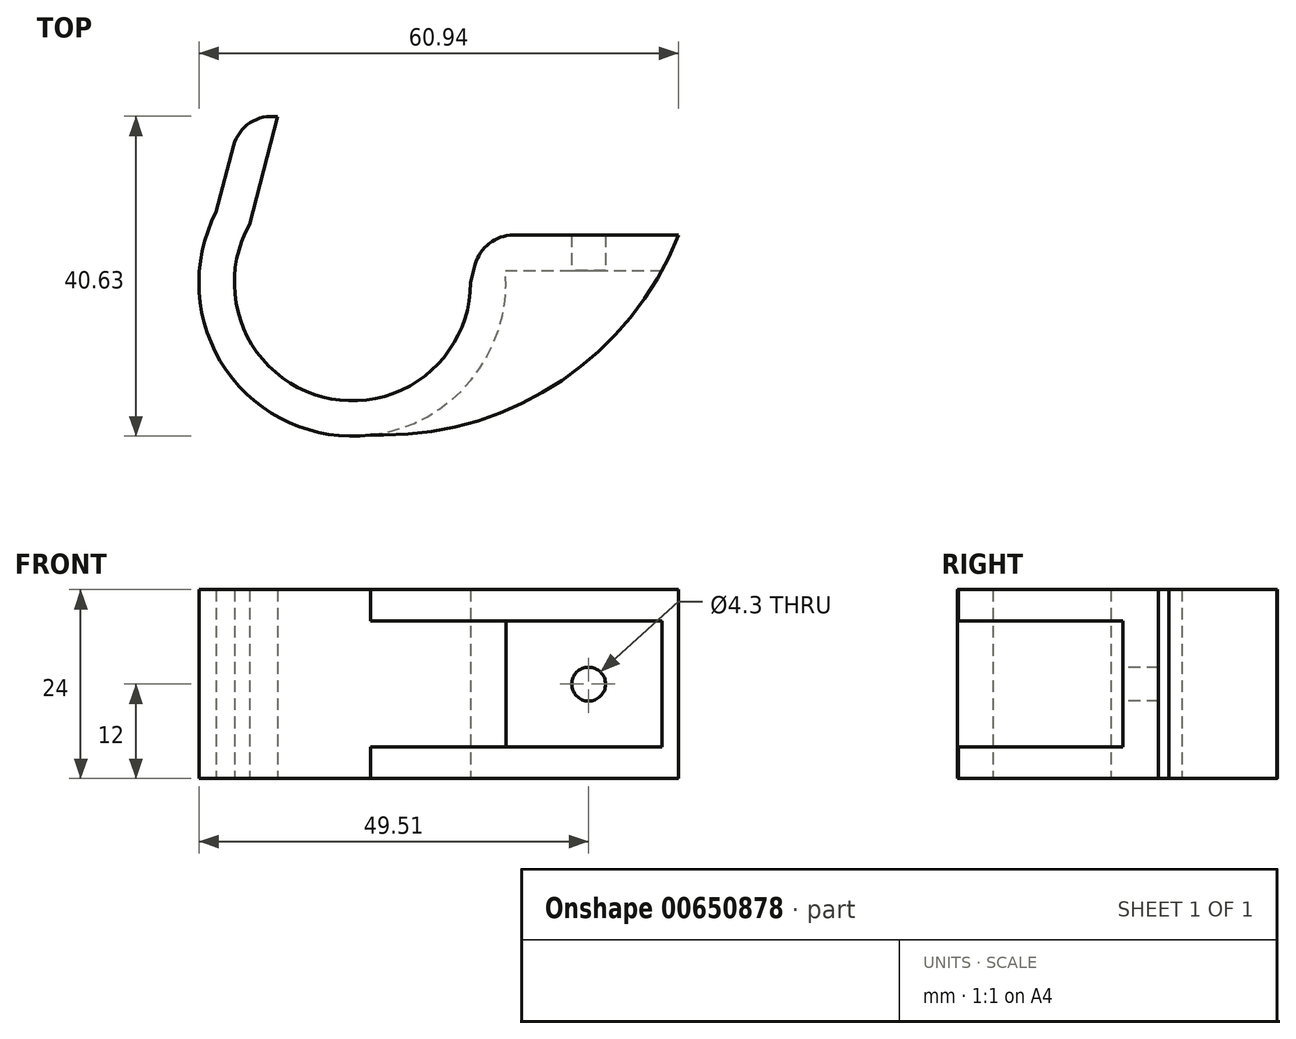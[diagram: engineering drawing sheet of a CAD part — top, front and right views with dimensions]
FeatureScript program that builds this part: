
annotation { "Feature Type Name" : "Feature", "Feature Type Description" : "" }
export const myFeature = defineFeature(function(context is Context, id is Id, definition is map)
    precondition{}
    {
        {
            var Q0;
            Q0=qCreatedBy(makeId("Top.planeOp"),FACE);
            var sketch = newSketch(context, id + "F0", { "sketchPlane" : qUnion([Q0])});
            skArc(sketch, "E0", {"start": v(-13.07, 7.36) * mm, "mid": v(-3.8, -14.5) * mm, "end": v(15, 0) * mm});
            skLineSegment(sketch, "E1", {"start": v(-13.07, 7.36) * mm, "end": v(-9.48, 21.07) * mm});
            skLineSegment(sketch, "E2", {"start": v(15, 0) * mm, "end": v(16.58, 6.03) * mm});
            skLineSegment(sketch, "E3", {"start": v(16.58, 6.03) * mm, "end": v(41.44, 6.03) * mm});
            skPoint(sketch, "E4.orphan", {"position": v(-15, 0) * mm});
            skLineSegment(sketch, "E5.0", {"start": v(-17.29, 9.02) * mm, "end": v(-13.83, 22.2) * mm});
            skArc(sketch, "E5.1", {"start": v(-17.29, 9.02) * mm, "mid": v(-3.9, -19.1) * mm, "end": v(19.44, 1.53) * mm});
            skLineSegment(sketch, "E5.2", {"start": v(19.44, 1.53) * mm, "end": v(41.44, 1.53) * mm});
            skLineSegment(sketch, "E6", {"start": v(41.44, 6.03) * mm, "end": v(41.44, 1.53) * mm});
            skLineSegment(sketch, "E7", {"start": v(-13.83, 22.2) * mm, "end": v(-9.48, 21.07) * mm});
            skSolve(sketch);
        }
        {
            var Q0;
            Q0=makeQuery(id+"F0.imprint","IMPRINT",FACE,{"disambiguationData":[TD([[makeQuery(id+"F0.imprint","IMPRINT",EDGE,{"derivedFrom":sQuery(id+"F0.wireOp",EDGE,"E0")}),-1.0]])]});
            extrude(context, id + "F1", {"entities" : qUnion([Q0]), "depth" : 24 * mm, "offsetDistance" : 25 * mm});
        }
        {
            var Q0;
            Q0=makeQuery(id+"F1.opExtrude","SWEPT_FACE",FACE,{"disambiguationData":[OSD([sQuery(id+"F0.wireOp",EDGE,"E5.2")])]});
            cPlane(context, id + "F2", {"entities" : qUnion([Q0]), "cplaneType" : CPlaneType.OFFSET, "offset" : 20.9 * mm, "width" : 150 * mm, "height" : 150 * mm});
        }
        {
            var Q0;
            Q0=qCreatedBy(id+"F2.planeOp",FACE);
            var sketch = newSketch(context, id + "F3", { "sketchPlane" : qUnion([Q0])});
            skLineSegment(sketch, "E8.0", {"start": v(0, 24) * mm, "end": v(41.44, 24) * mm});
            skLineSegment(sketch, "E9.0", {"start": v(41.44, 24) * mm, "end": v(41.44, 0) * mm});
            skLineSegment(sketch, "E10.0", {"start": v(0, 0) * mm, "end": v(41.44, 0) * mm});
            skLineSegment(sketch, "E11", {"start": v(0, 0) * mm, "end": v(0, 24) * mm});
            skPoint(sketch, "E12.orphan", {"position": v(19.44, 0) * mm});
            skPoint(sketch, "E13.orphan", {"position": v(19.44, 24) * mm});
            skLineSegment(sketch, "E14", {"start": v(41.44, 12) * mm, "end": v(0, 12) * mm, "construction": true});
            skPoint(sketch, "E15", {"position": v(20.72, 12) * mm});
            skLineSegment(sketch, "E16.bottom", {"start": v(41.44, 20) * mm, "end": v(0, 20) * mm});
            skLineSegment(sketch, "E16.top", {"start": v(41.44, 4) * mm, "end": v(0, 4) * mm});
            skLineSegment(sketch, "E16.left", {"start": v(41.44, 20) * mm, "end": v(41.44, 4) * mm});
            skLineSegment(sketch, "E16.right", {"start": v(0, 20) * mm, "end": v(0, 4) * mm});
            skSolve(sketch);
        }
        {
            var Q0;
            {var subQ0=sQuery(id+"F3.wireOp",EDGE,"E10.0");Q0=makeQuery(id+"F3.imprint","IMPRINT",FACE,{"disambiguationData":[TD([[makeQuery(id+"F3.imprint","IMPRINT",EDGE,{"derivedFrom":subQ0}),1.0]])]});}
            var Q1;
            {var subQ0=sQuery(id+"F3.wireOp",EDGE,"E8.0");Q1=makeQuery(id+"F3.imprint","IMPRINT",FACE,{"disambiguationData":[TD([[makeQuery(id+"F3.imprint","IMPRINT",EDGE,{"derivedFrom":subQ0}),-1.0]])]});}
            extrude(context, id + "F4", {"entities" : qUnion([Q0, Q1]), "operationType" : NewBodyOperationType.ADD, "oppositeDirection" : true, "depth" : 25 * mm, "offsetDistance" : 25 * mm});
        }
        {
            var Q0;
            {var subQ0=sQuery(id+"F3.wireOp",EDGE,"E16.bottom");Q0=makeQuery(id+"F4.boolean.opBoolean","SPLIT",FACE,{"disambiguationData":[TD([makeQuery(id+"F1.opExtrude","SWEPT_FACE",FACE,{"disambiguationData":[OSD([sQuery(id+"F0.wireOp",EDGE,"E0")])]})])],"derivedFrom":makeQuery(id+"F4.opExtrude","SWEPT_FACE",FACE,{"disambiguationData":[OSD([subQ0])]})});}
            extrude(context, id + "F5", {"entities" : qUnion([Q0]), "operationType" : NewBodyOperationType.REMOVE, "oppositeDirection" : true, "depth" : 25 * mm, "offsetDistance" : 25 * mm});
        }
        {
            var Q0;
            {var subQ0=sQuery(id+"F3.wireOp",EDGE,"E16.top");Q0=makeQuery(id+"F4.boolean.opBoolean","SPLIT",FACE,{"disambiguationData":[TD([makeQuery(id+"F1.opExtrude","SWEPT_FACE",FACE,{"disambiguationData":[OSD([sQuery(id+"F0.wireOp",EDGE,"E0")])]})])],"derivedFrom":makeQuery(id+"F4.opExtrude","SWEPT_FACE",FACE,{"disambiguationData":[OSD([subQ0])]})});}
            extrude(context, id + "F6", {"entities" : qUnion([Q0]), "operationType" : NewBodyOperationType.REMOVE, "oppositeDirection" : true, "depth" : 25 * mm, "offsetDistance" : 25 * mm});
        }
        {
            var Q0;
            {var subQ0=sQuery(id+"F3.wireOp",EDGE,"E9.0");Q0=makeQuery(id+"F4.opExtrude","CAP_EDGE",EDGE,{"disambiguationData":[OSD([subQ0]),TDD([makeQuery(id+"F3.imprint","IMPRINT",EDGE,{"disambiguationData":[TD([[makeQuery(id+"F3.imprint","INTERSECT",VERTEX,{"derivedFrom":[sQuery(id+"F3.wireOp",EDGE,"E8.0"),subQ0]}),-1.0]])],"derivedFrom":subQ0})])],"isStart":true});}
            var Q1;
            {var subQ0=sQuery(id+"F3.wireOp",EDGE,"E9.0");Q1=makeQuery(id+"F4.opExtrude","CAP_EDGE",EDGE,{"disambiguationData":[OSD([subQ0]),TDD([makeQuery(id+"F3.imprint","IMPRINT",EDGE,{"disambiguationData":[TD([[makeQuery(id+"F3.imprint","INTERSECT",VERTEX,{"derivedFrom":[subQ0,sQuery(id+"F3.wireOp",EDGE,"E10.0")]}),1.0]])],"derivedFrom":subQ0})])],"isStart":true});}
            fillet(context, id + "F7", {"entities" : qUnion([Q0, Q1]), "radius" : 40.32 * mm, "tangentPropagation" : true, "allowEdgeOverflow" : false});
        }
        {
            var Q0;
            Q0=makeQuery(id+"F1.opExtrude","SWEPT_EDGE",EDGE,{"disambiguationData":[OSD([sQuery(id+"F0.wireOp",EDGE,"E2"),sQuery(id+"F0.wireOp",EDGE,"E3")])]});
            fillet(context, id + "F8", {"entities" : qUnion([Q0]), "radius" : 5 * mm, "tangentPropagation" : true, "allowEdgeOverflow" : false});
        }
        {
            var Q0;
            Q0=makeQuery(id+"F1.opExtrude","SWEPT_EDGE",EDGE,{"disambiguationData":[OSD([sQuery(id+"F0.wireOp",EDGE,"E5.0"),sQuery(id+"F0.wireOp",EDGE,"E7")])]});
            fillet(context, id + "F9", {"entities" : qUnion([Q0]), "radius" : 5 * mm, "tangentPropagation" : true, "allowEdgeOverflow" : false});
        }
        {
            var Q0;
            Q0=makeQuery(id+"F1.opExtrude","SWEPT_FACE",FACE,{"disambiguationData":[OSD([sQuery(id+"F0.wireOp",EDGE,"E5.2")])]});
            var sketch = newSketch(context, id + "F10", { "sketchPlane" : qUnion([Q0])});
            skLineSegment(sketch, "E17", {"start": v(19.44, 12) * mm, "end": v(39.32, 12) * mm, "construction": true});
            skPoint(sketch, "E18", {"position": v(30.01, 12) * mm});
            skSolve(sketch);
        }
        {
            var Q0;
            Q0=sQuery(id+"F10.wireOp",VERTEX,"E18");
            var Q1;
            Q1=makeQuery(id+"F1.opExtrude","SWEPT_BODY",BODY,{"disambiguationData":[OSD([sQuery(id+"F0.wireOp",EDGE,"E0"),sQuery(id+"F0.wireOp",EDGE,"E1"),sQuery(id+"F0.wireOp",EDGE,"E2"),sQuery(id+"F0.wireOp",EDGE,"E3"),sQuery(id+"F0.wireOp",EDGE,"E5.0"),sQuery(id+"F0.wireOp",EDGE,"E5.1"),sQuery(id+"F0.wireOp",EDGE,"E5.2"),sQuery(id+"F0.wireOp",EDGE,"E6"),sQuery(id+"F0.wireOp",EDGE,"E7")])]});
            hole(context, id + "F11", {"style" : HoleStyle.SIMPLE, "endStyle" : HoleEndStyle.THROUGH, "holeDiameter" : 4.3 * mm, "majorDiameter" : 5 * mm, "isTappedThrough" : true, "tappedDepth" : 12 * mm, "tapClearance" : 3, "locations" : qUnion([Q0]), "scope" : qUnion([Q1])});
        }
    });
